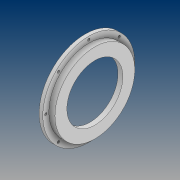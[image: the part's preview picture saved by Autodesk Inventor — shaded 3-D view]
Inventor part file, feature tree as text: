
AUTODESK INVENTOR PART (.ipt)
format: ipt  version: 2021 (Build 250183000, 183)  size: 197,120 bytes
history: native  units: mm
features: thread x8, sketch x4, extrude x3, pattern_circular x1, revolve x1
ambient origin geometry x8: Origin, YZ Plane, XZ Plane, XY Plane, X Axis, Y Axis, Z Axis, Center Point
bodies: Solid1 (feature_tree)
feature tree (17):
  extrude  "Extrusion1"  Depth=327.8mm
  extrude  "Extrusion2"  Depth=15.0mm
  pattern_circular  "Circular Pattern1"  Count=8 Angle=360.0deg
  extrude  "Extrusion3"  Depth=15.0mm
  revolve  "Revolution1"  [1 undecoded]
  thread  "Thread1"  [1 undecoded]
  thread  "Thread2"  [1 undecoded]
  thread  "Thread3"  [1 undecoded]
  thread  "Thread4"  [1 undecoded]
  thread  "Thread5"  [1 undecoded]
  thread  "Thread6"  [1 undecoded]
  thread  "Thread7"  [1 undecoded]
  thread  "Thread8"  [1 undecoded]
  sketch  "Sketch1"  dims[d0=377.8mm d2=327.8mm]
  sketch  "Sketch2"  dims[d3=15.0mm d4=0.0mm d5=353.0mm]
  sketch  "Sketch3"  dims[d6=10.0mm]
  sketch  "Sketch4"  dims[d7=0.0mm d8=0.0mm d9=80.0mm d10=360.0deg d12=317.8mm d13=40.0mm d14=0.0mm d15=90.0deg d16=15.0mm d17=0.0mm d18=15.0mm d19=0.0mm d20=15.0mm d21=0.0mm d22=15.0mm d23=0.0mm d24=15.0mm d25=0.0mm d26=15.0mm d27=0.0mm d28=15.0mm d29=0.0mm d30=15.0mm d31=0.0mm]
note: 9 required parameter values undecoded (feature->parameter linkage not recoverable at this tier; creation-order binding heuristic only, values carry confidence <= 0.55)